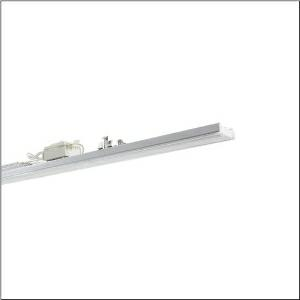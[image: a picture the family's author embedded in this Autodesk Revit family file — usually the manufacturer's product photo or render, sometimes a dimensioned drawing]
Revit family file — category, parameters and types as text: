
# Revit family: licross_r__11_recessed_ho_51te12dn4exm3s_86d7
name_source: partatom
category: Lighting Fixtures
units: mm (PartAtom-declared; Revit-internal decimal feet)

## family parameters
Cut with Voids When Loaded = No
Host = Face
Light Source = No
Part Type = Normal
Room Calculation Point = No
Round Connector Dimension = Use Diameter
Shared = No

## types (1)
- --- (1 x LED, 1000 lm, 7.2 W, 4000K)
    Apparent Load = 7 VA
    CIE Flux Codes = 66 91 98 100 100
    Color Rendering = 80
    Color Temperature = 4000K
    Default Elevation = 1800 mm
    Description = Licross® 11 Recessed HO, luminaire insert, of sheet steel, galvanised, coil coated, white, length: 1.500mm, width: 66mm, height: 67mm, LED rated luminous flux: 14.030lm, light colour: 840, control gear: DALI 2 (for two DALI lines), with plug, 6-pole, with phase selection, for trunking rail, 14-core, mains connection: 220..240V, AC, 50/60Hz, rated input power: 81W, for trunking rail, 14-core, internal wiring halogen-free, for emergency light function, converter,control gear: single battery element, battery: LiFePO4, 9Ah, primary optical cover: cover, of PMMA, light emission: direct distribution, primary light characteristic: symmetric, protection rating (complete): IP54, insulation class (complete): insulation class I (protective earthing), certification: CE, UKCA, protection symbol: D if used in an environment with non-conductive dust loads with corresponding accessories, impact resistance: IK06, permissible ambient temperature for indoor applications: +5..+30°C, standard: EN 60598-2-22, LABS conformity tested according to VDMA 24364:2018-05, reducing of maximum allowable ambient temperature of 5°C with ceiling mounting, corresponds to IFS (International Featured Standards) requirements for safety and quality in the food industry, packaging unit: 1 piece
    Height = 58 mm
    Lamp = 1 x LED
    Lamp Light Flux = 1000 lm
    Lamp Power = 7.2 W
    Lamp count = 1
    Length = 1500 mm
    Luminous efficacy = 139 lm/W
    Manufacturer = Siteco
    ModVariant = No
    Model = 51TE12DN4EXM3S
    Mounting Place = Ceiling
    Mounting Type = Pendant
    Number of Poles = 1
    OnlyDefault = Yes
    Power Factor = 1
    Product Name = Licross® 11 Recessed HO
    Product group = luminaire insert | ceiling pendant
    ProductGroupID = 902
    Protection Class = Protection class I
    Protection Degree = IP 54
    RLX_Detail_Level = 1
    RLX_Emergency_Light_Flux = 0 lm
    RLX_Emergency_Type = 0
    RLX_Emergency_Type_DB = No
    RlxData = <blob elided: 25017 chars, md5=d6d9283d>
    Socket = socket
    Standby Power = 0 W
    System Light Flux = 1000 lm
    System Power = 7 W
    Type Comments = : emergency light operation: 3 h
    Type Image = l_1296930.jpg
    URL = http://relux.com
    VarID = @adj_111593
    Voltage = 0 V
    Weight = 0.00 kg
    Width = 66 mm

## geometry (parser evidence)
native form markers: Blend x4, Sweep x10
no freeform markers — native parametric forms only
